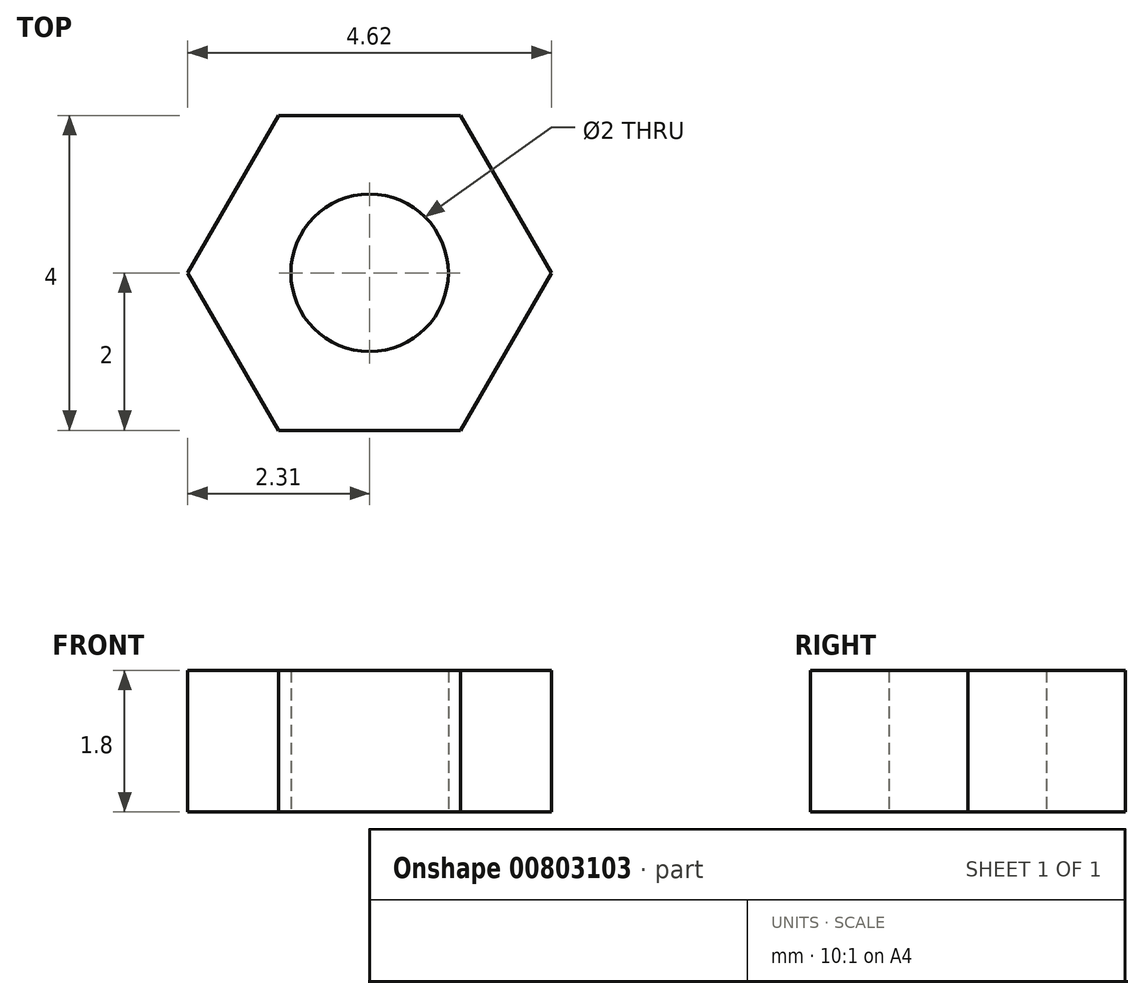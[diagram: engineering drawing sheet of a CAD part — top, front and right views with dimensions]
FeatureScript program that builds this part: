
annotation { "Feature Type Name" : "Feature", "Feature Type Description" : "" }
export const myFeature = defineFeature(function(context is Context, id is Id, definition is map)
    precondition{}
    {
        {
            var Q0;
            Q0=qCreatedBy(makeId("Top.planeOp"),FACE);
            var sketch = newSketch(context, id + "F0", { "sketchPlane" : qUnion([Q0])});
            skCircle(sketch, "E0.cCircle", {"center": v(0, 0) * mm, "radius": 2 * mm, "construction": true});
            skLineSegment(sketch, "E0.0", {"start": v(2.3, 0) * mm, "end": v(1.15, -2) * mm});
            skLineSegment(sketch, "E0.1", {"start": v(1.15, -2) * mm, "end": v(-1.15, -2) * mm});
            skLineSegment(sketch, "E0.2", {"start": v(-1.15, -2) * mm, "end": v(-2.3, 0) * mm});
            skLineSegment(sketch, "E0.3", {"start": v(-2.3, 0) * mm, "end": v(-1.15, 2) * mm});
            skLineSegment(sketch, "E0.4", {"start": v(-1.15, 2) * mm, "end": v(1.15, 2) * mm});
            skLineSegment(sketch, "E0.5", {"start": v(1.15, 2) * mm, "end": v(2.3, 0) * mm});
            skPoint(sketch, "E0.0.midPoint", {"position": v(1.73, -1) * mm});
            skCircle(sketch, "E1", {"center": v(0, 0) * mm, "radius": 1 * mm});
            skSolve(sketch);
        }
        {
            var Q0;
            Q0 = qSketchRegion(id + "F0", true);
            extrude(context, id + "F1", {"entities" : qUnion([Q0]), "depth" : 1.8 * mm, "offsetDistance" : 25 * mm});
        }
    });
